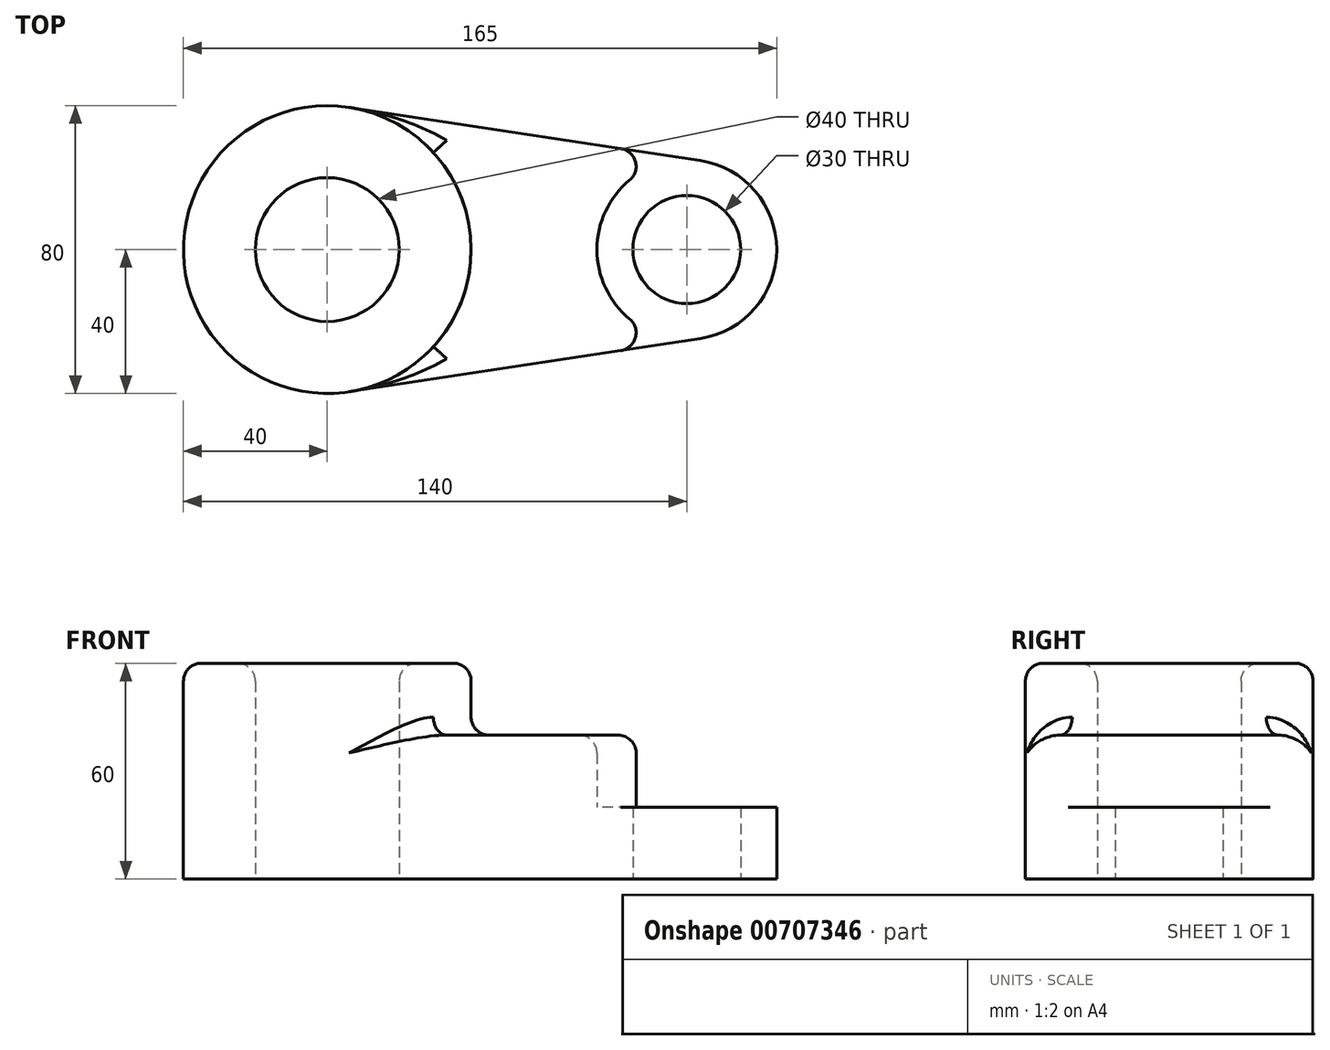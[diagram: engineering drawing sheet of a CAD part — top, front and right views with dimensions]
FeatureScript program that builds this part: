
annotation { "Feature Type Name" : "Feature", "Feature Type Description" : "" }
export const myFeature = defineFeature(function(context is Context, id is Id, definition is map)
    precondition{}
    {
        {
            var Q0;
            Q0=qCreatedBy(makeId("Top.planeOp"),FACE);
            var sketch = newSketch(context, id + "F0", { "sketchPlane" : qUnion([Q0])});
            skCircle(sketch, "E0", {"center": v(-50, 0) * mm, "radius": 40 * mm});
            skCircle(sketch, "E1", {"center": v(50, 0) * mm, "radius": 25 * mm});
            skCircle(sketch, "E2", {"center": v(-50, 0) * mm, "radius": 20 * mm});
            skCircle(sketch, "E3", {"center": v(50, 0) * mm, "radius": 15 * mm});
            skLineSegment(sketch, "E4", {"start": v(-44, 39.55) * mm, "end": v(53.75, 24.72) * mm});
            skLineSegment(sketch, "E5", {"start": v(-44, -39.55) * mm, "end": v(53.75, -24.72) * mm});
            skSolve(sketch);
        }
        {
            var Q0;
            Q0=makeQuery(id+"F0.imprint","IMPRINT",FACE,{"disambiguationData":[TD([[makeQuery(id+"F0.imprint","IMPRINT",EDGE,{"derivedFrom":sQuery(id+"F0.wireOp",EDGE,"E2")}),-1.0]])]});
            extrude(context, id + "F1", {"entities" : qUnion([Q0]), "depth" : 60 * mm, "offsetDistance" : 25 * mm});
        }
        {
            var Q0;
            {var subQ0=sQuery(id+"F0.wireOp",EDGE,"E4");Q0=makeQuery(id+"F0.imprint","IMPRINT",FACE,{"disambiguationData":[TD([[makeQuery(id+"F0.imprint","IMPRINT",EDGE,{"derivedFrom":subQ0}),-1.0]])]});}
            extrude(context, id + "F2", {"entities" : qUnion([Q0]), "operationType" : NewBodyOperationType.ADD, "depth" : 40 * mm, "offsetDistance" : 25 * mm});
        }
        {
            var Q0;
            Q0=makeQuery(id+"F0.imprint","IMPRINT",FACE,{"disambiguationData":[TD([[makeQuery(id+"F0.imprint","IMPRINT",EDGE,{"derivedFrom":sQuery(id+"F0.wireOp",EDGE,"E3")}),-1.0]])]});
            extrude(context, id + "F3", {"entities" : qUnion([Q0]), "operationType" : NewBodyOperationType.ADD, "depth" : 20 * mm, "offsetDistance" : 25 * mm});
        }
        {
            var Q0;
            Q0=makeQuery(id+"F1.opExtrude","CAP_FACE",FACE,{"disambiguationData":[OSD([sQuery(id+"F0.wireOp",EDGE,"E0"),sQuery(id+"F0.wireOp",EDGE,"E2")])],"isStart":false});
            var Q1;
            Q1=makeQuery(id+"F2.opExtrude","CAP_FACE",FACE,{"disambiguationData":[OSD([sQuery(id+"F0.wireOp",EDGE,"E0"),sQuery(id+"F0.wireOp",EDGE,"E1"),sQuery(id+"F0.wireOp",EDGE,"E4"),sQuery(id+"F0.wireOp",EDGE,"E5")])],"isStart":false});
            var Q2;
            {var subQ0=sQuery(id+"F0.wireOp",EDGE,"E1");var subQ1=sQuery(id+"F0.wireOp",EDGE,"E4");Q2=makeQuery(id+"F3.boolean.opBoolean","SPLIT",EDGE,{"disambiguationData":[topologyDisambiguationEdgeConnected([makeQuery(id+"F2.opExtrude","SWEPT_FACE",FACE,{"disambiguationData":[OSD([subQ0])]})])],"derivedFrom":makeQuery(id+"F2.opExtrude","SWEPT_EDGE",EDGE,{"disambiguationData":[OSD([subQ0,subQ1])]})});}
            var Q3;
            {var subQ0=sQuery(id+"F0.wireOp",EDGE,"E1");var subQ1=sQuery(id+"F0.wireOp",EDGE,"E5");Q3=makeQuery(id+"F3.boolean.opBoolean","SPLIT",EDGE,{"disambiguationData":[topologyDisambiguationEdgeConnected([makeQuery(id+"F2.opExtrude","SWEPT_FACE",FACE,{"disambiguationData":[OSD([subQ0])]})])],"derivedFrom":makeQuery(id+"F2.opExtrude","SWEPT_EDGE",EDGE,{"disambiguationData":[OSD([subQ0,subQ1])]})});}
            fillet(context, id + "F4", {"entities" : qUnion([Q0, Q1, Q2, Q3]), "radius" : 5 * mm, "tangentPropagation" : true, "allowEdgeOverflow" : false});
        }
    });
